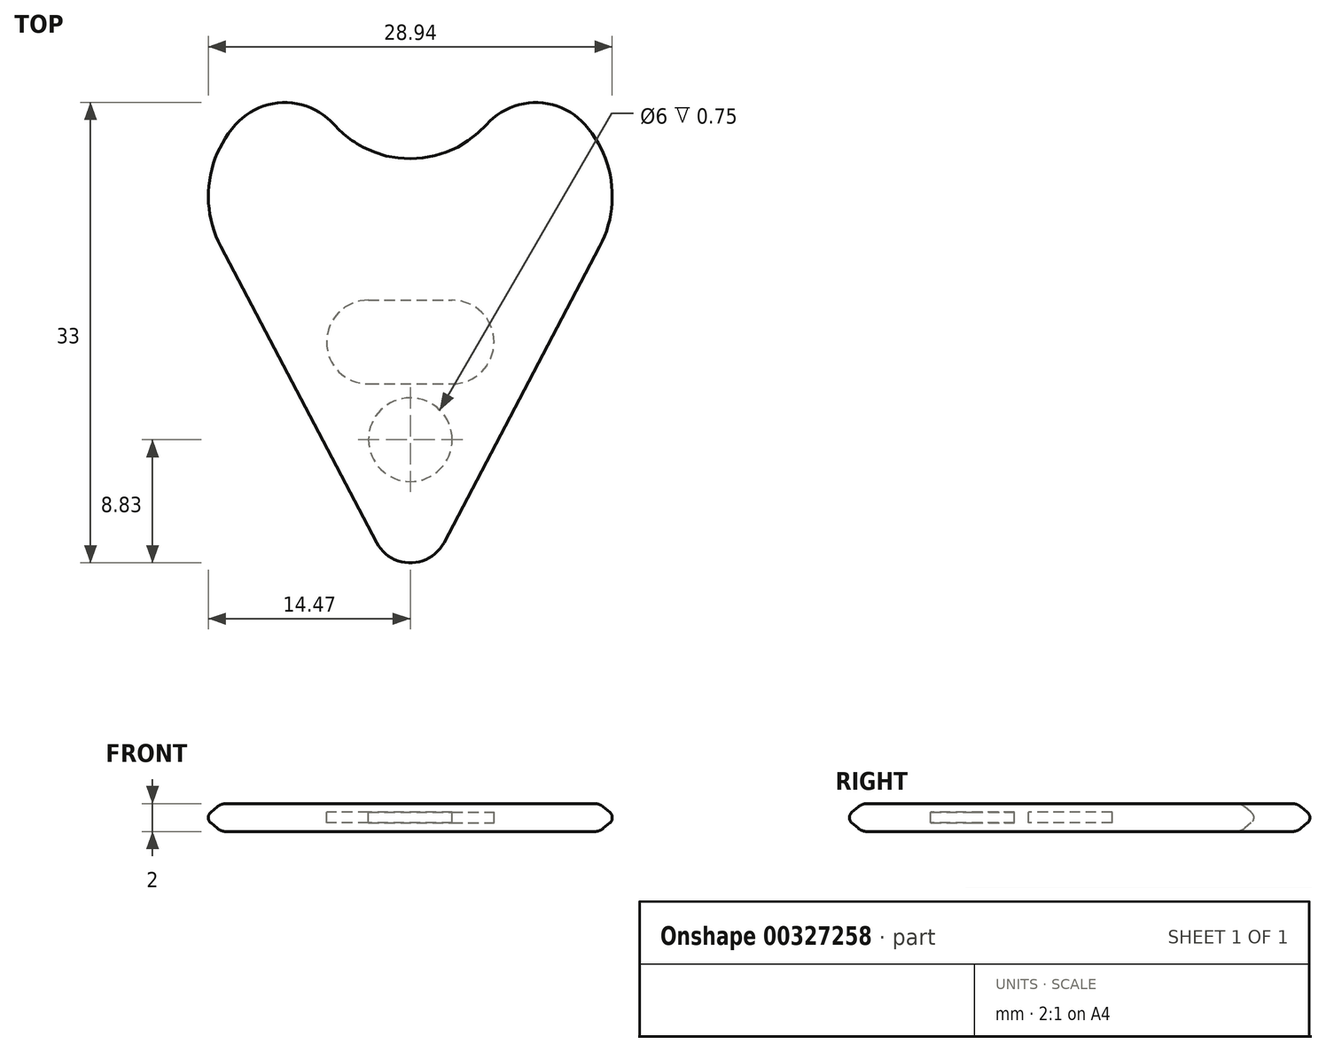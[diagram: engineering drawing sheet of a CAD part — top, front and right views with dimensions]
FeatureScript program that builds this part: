
annotation { "Feature Type Name" : "Feature", "Feature Type Description" : "" }
export const myFeature = defineFeature(function(context is Context, id is Id, definition is map)
    precondition{}
    {
        {
            var Q0;
            Q0=qCreatedBy(makeId("Top.planeOp"),FACE);
            var sketch = newSketch(context, id + "F0", { "sketchPlane" : qUnion([Q0])});
            skLineSegment(sketch, "E0", {"start": v(-6.75, 12.45) * mm, "end": v(6.75, 12.45) * mm});
            skLineSegment(sketch, "E1", {"start": v(13.83, 0.73) * mm, "end": v(2.65, -20.5) * mm});
            skLineSegment(sketch, "E2", {"start": v(-2.65, -20.5) * mm, "end": v(-13.83, 0.73) * mm});
            skPoint(sketch, "E3.visualSharp", {"position": v(-20, 12.45) * mm});
            skArc(sketch, "E3.filletArc", {"start": v(-6.75, 12.45) * mm, "mid": v(-13.6, 8.59) * mm, "end": v(-13.83, 0.73) * mm});
            skPoint(sketch, "E4.visualSharp", {"position": v(20, 12.45) * mm});
            skArc(sketch, "E4.filletArc", {"start": v(13.83, 0.73) * mm, "mid": v(13.6, 8.59) * mm, "end": v(6.75, 12.45) * mm});
            skPoint(sketch, "E5.visualSharp", {"position": v(0, -25.55) * mm});
            skArc(sketch, "E5.filletArc", {"start": v(-2.65, -20.5) * mm, "mid": v(0, -22.1) * mm, "end": v(2.65, -20.5) * mm});
            skSolve(sketch);
        }
        {
            var Q0;
            Q0=makeQuery(id+"F0.imprint","IMPRINT",FACE,{"disambiguationData":[TD([[makeQuery(id+"F0.imprint","IMPRINT",EDGE,{"derivedFrom":sQuery(id+"F0.wireOp",EDGE,"E0")}),-1.0]])]});
            extrude(context, id + "F1", {"entities" : qUnion([Q0]), "endBound" : BoundingType.SYMMETRIC, "depth" : 2 * mm});
        }
        {
            var Q0;
            Q0=makeQuery(id+"F1.opExtrude","CAP_FACE",FACE,{"disambiguationData":[OSD([sQuery(id+"F0.wireOp",EDGE,"E0"),sQuery(id+"F0.wireOp",EDGE,"E1"),sQuery(id+"F0.wireOp",EDGE,"E2"),sQuery(id+"F0.wireOp",EDGE,"E3.filletArc"),sQuery(id+"F0.wireOp",EDGE,"E4.filletArc"),sQuery(id+"F0.wireOp",EDGE,"E5.filletArc")])],"isStart":false});
            var sketch = newSketch(context, id + "F2", { "sketchPlane" : qUnion([Q0])});
            skArc(sketch, "E6", {"start": v(-6.75, 12.45) * mm, "mid": v(0, 7.42) * mm, "end": v(6.75, 12.45) * mm});
            skLineSegment(sketch, "E7.0", {"start": v(-6.75, 12.45) * mm, "end": v(6.75, 12.45) * mm});
            skSolve(sketch);
        }
        {
            var Q0;
            Q0 = qSketchRegion(id + "F2", true);
            extrude(context, id + "F3", {"entities" : qUnion([Q0]), "operationType" : NewBodyOperationType.REMOVE, "oppositeDirection" : true, "depth" : 25 * mm});
        }
        {
            var Q0;
            {var subQ0=sQuery(id+"F0.wireOp",EDGE,"E3.filletArc");Q0=makeQuery(id+"F3.boolean.opBoolean","MERGE",EDGE,{"derivedFrom":[makeQuery(id+"F1.opExtrude","SWEPT_EDGE",EDGE,{"disambiguationData":[OSD([sQuery(id+"F0.wireOp",EDGE,"E0"),subQ0])]}),makeQuery(id+"F3.opExtrude","SWEPT_EDGE",EDGE,{"disambiguationData":[OSD([subQ0,sQuery(id+"F2.wireOp",EDGE,"E6"),sQuery(id+"F2.wireOp",EDGE,"E7.0")])]})]});}
            var Q1;
            {var subQ0=sQuery(id+"F0.wireOp",EDGE,"E4.filletArc");Q1=makeQuery(id+"F3.boolean.opBoolean","MERGE",EDGE,{"derivedFrom":[makeQuery(id+"F1.opExtrude","SWEPT_EDGE",EDGE,{"disambiguationData":[OSD([sQuery(id+"F0.wireOp",EDGE,"E0"),subQ0])]}),makeQuery(id+"F3.opExtrude","SWEPT_EDGE",EDGE,{"disambiguationData":[OSD([subQ0,sQuery(id+"F2.wireOp",EDGE,"E6"),sQuery(id+"F2.wireOp",EDGE,"E7.0")])]})]});}
            fillet(context, id + "F4", {"entities" : qUnion([Q0, Q1]), "radius" : 5 * mm, "tangentPropagation" : true, "allowEdgeOverflow" : false});
        }
        {
            var Q0;
            Q0=makeQuery(id+"F1.opExtrude","CAP_EDGE",EDGE,{"disambiguationData":[OSD([sQuery(id+"F0.wireOp",EDGE,"E1")])],"isStart":false});
            var Q1;
            Q1=makeQuery(id+"F1.opExtrude","CAP_EDGE",EDGE,{"disambiguationData":[OSD([sQuery(id+"F0.wireOp",EDGE,"E1")])],"isStart":true});
            chamfer(context, id + "F5", {"entities" : qUnion([Q0, Q1]), "chamferType" : ChamferType.OFFSET_ANGLE, "width" : 1 * mm, "oppositeDirection" : false, "angle" : 50 * degree, "tangentPropagation" : true});
        }
        {
            var Q0;
            {var subQ0=sQuery(id+"F0.wireOp",EDGE,"E2");Q0=makeQuery(id+"F5.opChamfer","BLEND_EDGE",EDGE,{"blendedFrom":[makeQuery(id+"F1.opExtrude","CAP_EDGE",EDGE,{"disambiguationData":[OSD([subQ0])],"isStart":false}),makeQuery(id+"F1.opExtrude","CAP_FACE",FACE,{"disambiguationData":[OSD([sQuery(id+"F0.wireOp",EDGE,"E0"),sQuery(id+"F0.wireOp",EDGE,"E1"),subQ0,sQuery(id+"F0.wireOp",EDGE,"E3.filletArc"),sQuery(id+"F0.wireOp",EDGE,"E4.filletArc"),sQuery(id+"F0.wireOp",EDGE,"E5.filletArc")])],"isStart":false})],"blendedInto":[makeQuery(id+"F1.opExtrude","CAP_FACE",FACE,{"disambiguationData":[OSD([sQuery(id+"F0.wireOp",EDGE,"E0"),sQuery(id+"F0.wireOp",EDGE,"E1"),subQ0,sQuery(id+"F0.wireOp",EDGE,"E3.filletArc"),sQuery(id+"F0.wireOp",EDGE,"E4.filletArc"),sQuery(id+"F0.wireOp",EDGE,"E5.filletArc")])],"isStart":false})]});}
            var Q1;
            {var subQ0=sQuery(id+"F0.wireOp",EDGE,"E1");Q1=makeQuery(id+"F5.opChamfer","BLEND_EDGE",EDGE,{"blendedFrom":[makeQuery(id+"F1.opExtrude","CAP_EDGE",EDGE,{"disambiguationData":[OSD([subQ0])],"isStart":true}),makeQuery(id+"F1.opExtrude","CAP_FACE",FACE,{"disambiguationData":[OSD([sQuery(id+"F0.wireOp",EDGE,"E0"),subQ0,sQuery(id+"F0.wireOp",EDGE,"E2"),sQuery(id+"F0.wireOp",EDGE,"E3.filletArc"),sQuery(id+"F0.wireOp",EDGE,"E4.filletArc"),sQuery(id+"F0.wireOp",EDGE,"E5.filletArc")])],"isStart":true})],"blendedInto":[makeQuery(id+"F1.opExtrude","CAP_FACE",FACE,{"disambiguationData":[OSD([sQuery(id+"F0.wireOp",EDGE,"E0"),subQ0,sQuery(id+"F0.wireOp",EDGE,"E2"),sQuery(id+"F0.wireOp",EDGE,"E3.filletArc"),sQuery(id+"F0.wireOp",EDGE,"E4.filletArc"),sQuery(id+"F0.wireOp",EDGE,"E5.filletArc")])],"isStart":true})]});}
            fillet(context, id + "F6", {"entities" : qUnion([Q0, Q1]), "radius" : 1 * mm, "tangentPropagation" : true, "allowEdgeOverflow" : false});
        }
        {
            var Q0;
            Q0=qCreatedBy(makeId("Top.planeOp"),FACE);
            var sketch = newSketch(context, id + "F7", { "sketchPlane" : qUnion([Q0])});
            skCircle(sketch, "E8", {"center": v(0, -13) * mm, "radius": 3 * mm});
            skArc(sketch, "E9", {"start": v(3, -9) * mm, "mid": v(6, -6) * mm, "end": v(3, -3) * mm});
            skArc(sketch, "E10", {"start": v(-3, -3) * mm, "mid": v(-6, -6) * mm, "end": v(-3, -9) * mm});
            skLineSegment(sketch, "E11", {"start": v(-3, -3) * mm, "end": v(3, -3) * mm});
            skLineSegment(sketch, "E12", {"start": v(-3, -9) * mm, "end": v(3, -9) * mm});
            skSolve(sketch);
        }
        {
            var Q0;
            Q0=qSketchRegion(id+"F7",true);
            extrude(context, id + "F8", {"entities" : qUnion([Q0]), "operationType" : NewBodyOperationType.REMOVE, "endBound" : BoundingType.SYMMETRIC, "oppositeDirection" : true, "depth" : 0.75 * mm});
        }
        {
            var Q0;
            {var subQ0=sQuery(id+"F0.wireOp",EDGE,"E2");Q0=makeQuery(id+"F5.opChamfer","BLEND_EDGE",EDGE,{"blendedFrom":[makeQuery(id+"F1.opExtrude","CAP_EDGE",EDGE,{"disambiguationData":[OSD([subQ0])],"isStart":true}),makeQuery(id+"F1.opExtrude","CAP_EDGE",EDGE,{"disambiguationData":[OSD([subQ0])],"isStart":false})],"blendedInto":[]});}
            fillet(context, id + "F9", {"entities" : qUnion([Q0]), "radius" : 0.5 * mm, "tangentPropagation" : true, "allowEdgeOverflow" : false});
        }
    });
